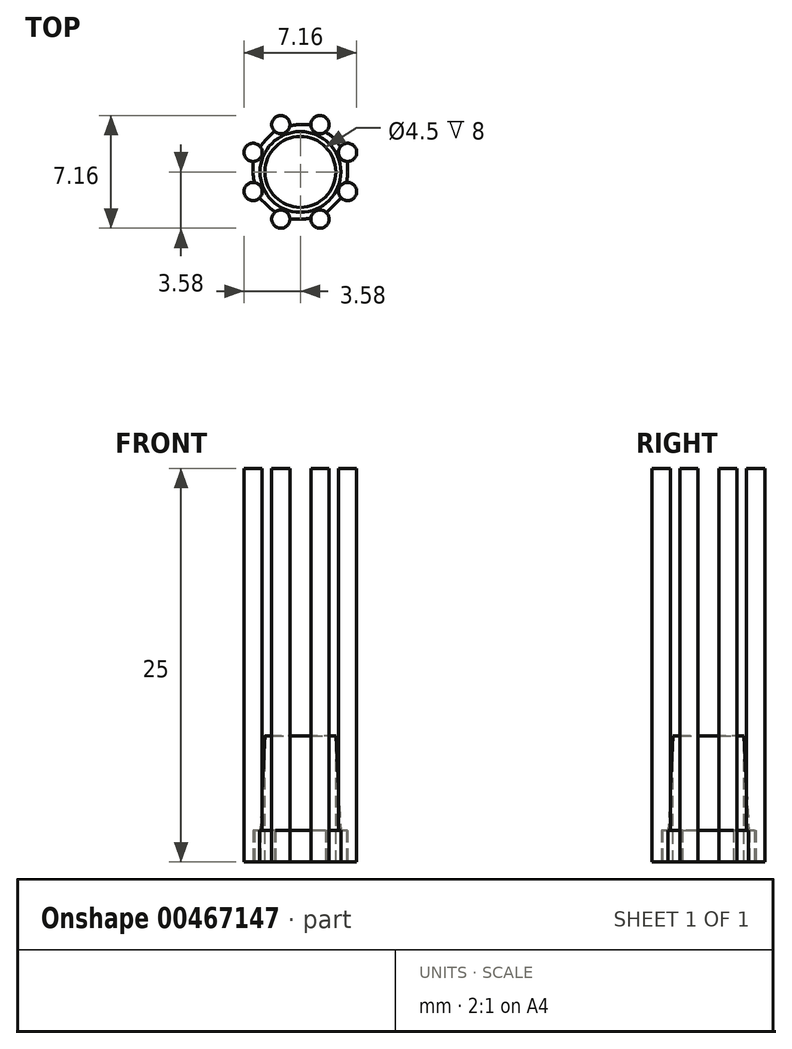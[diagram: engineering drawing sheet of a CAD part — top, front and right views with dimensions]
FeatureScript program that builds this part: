
annotation { "Feature Type Name" : "Feature", "Feature Type Description" : "" }
export const myFeature = defineFeature(function(context is Context, id is Id, definition is map)
    precondition{}
    {
        {
            var Q0;
            Q0=qCreatedBy(makeId("Top.planeOp"),FACE);
            var sketch = newSketch(context, id + "F0", { "sketchPlane" : qUnion([Q0])});
            skCircle(sketch, "E0", {"center": v(0, 0) * mm, "radius": 2.25 * mm});
            skSolve(sketch);
        }
        {
            var Q0;
            Q0=makeQuery(id+"F0.imprint","IMPRINT",FACE,{"disambiguationData":[TD([[makeQuery(id+"F0.imprint","IMPRINT",EDGE,{"derivedFrom":sQuery(id+"F0.wireOp",EDGE,"E0")}),1.0]])]});
            extrude(context, id + "F1", {"entities" : qUnion([Q0]), "oppositeDirection" : true, "depth" : 8 * mm, "offsetDistance" : 25 * mm, "hasDraft" : true, "draftAngle" : 3 * degree});
        }
        {
            var Q0;
            Q0=makeQuery(id+"F1.opExtrude","CAP_FACE",FACE,{"disambiguationData":[OSD([sQuery(id+"F0.wireOp",EDGE,"E0")])],"isStart":false});
            var sketch = newSketch(context, id + "F2", { "sketchPlane" : qUnion([Q0])});
            skCircle(sketch, "E1", {"center": v(0, 0) * mm, "radius": 3 * mm});
            skCircle(sketch, "E2.cCircle", {"center": v(0, 0) * mm, "radius": 3 * mm, "construction": true});
            skLineSegment(sketch, "E2.0", {"start": v(-1.24, -3) * mm, "end": v(-3, -1.24) * mm});
            skLineSegment(sketch, "E2.1", {"start": v(-3, -1.24) * mm, "end": v(-3, 1.24) * mm});
            skLineSegment(sketch, "E2.2", {"start": v(-3, 1.24) * mm, "end": v(-1.24, 3) * mm});
            skLineSegment(sketch, "E2.3", {"start": v(-1.24, 3) * mm, "end": v(1.24, 3) * mm});
            skLineSegment(sketch, "E2.4", {"start": v(1.24, 3) * mm, "end": v(3, 1.24) * mm});
            skLineSegment(sketch, "E2.5", {"start": v(3, 1.24) * mm, "end": v(3, -1.24) * mm});
            skLineSegment(sketch, "E2.6", {"start": v(3, -1.24) * mm, "end": v(1.24, -3) * mm});
            skLineSegment(sketch, "E2.7", {"start": v(1.24, -3) * mm, "end": v(-1.24, -3) * mm});
            skPoint(sketch, "E2.0.midPoint", {"position": v(-2.12, -2.12) * mm});
            skCircle(sketch, "E3", {"center": v(3, 1.24) * mm, "radius": 0.58 * mm});
            skCircle(sketch, "E4", {"center": v(1.24, 3) * mm, "radius": 0.58 * mm});
            skCircle(sketch, "E5", {"center": v(-1.24, 3) * mm, "radius": 0.58 * mm});
            skCircle(sketch, "E6", {"center": v(-3, 1.24) * mm, "radius": 0.58 * mm});
            skCircle(sketch, "E7", {"center": v(-3, -1.24) * mm, "radius": 0.58 * mm});
            skCircle(sketch, "E8", {"center": v(-1.24, -3) * mm, "radius": 0.58 * mm});
            skCircle(sketch, "E9", {"center": v(1.24, -3) * mm, "radius": 0.58 * mm});
            skCircle(sketch, "E10", {"center": v(3, -1.24) * mm, "radius": 0.58 * mm});
            skSolve(sketch);
        }
        {
            var Q0;
            Q0=makeQuery(id+"F2.imprint","IMPRINT",FACE,{"disambiguationData":[TD([[makeQuery(id+"F2.imprint","IMPRINT",EDGE,{"derivedFrom":sQuery(id+"F2.wireOp",EDGE,"E1")}),1.0]])]});
            var Q1;
            Q1=makeQuery(id+"F2.imprint","IMPRINT",FACE,{"disambiguationData":[TD([[makeQuery(id+"F2.imprint","IMPRINT",EDGE,{"derivedFrom":makeQuery(id+"F1.opExtrude","CAP_EDGE",EDGE,{"disambiguationData":[OSD([sQuery(id+"F0.wireOp",EDGE,"E0")])],"isStart":false})}),-1.0]])]});
            var Q2;
            {var subQ0=sQuery(id+"F2.wireOp",EDGE,"E2.4");var subQ1=sQuery(id+"F2.wireOp",EDGE,"E1");var subQ2=makeQuery(id+"F2.imprint","INTERSECT",VERTEX,{"derivedFrom":[subQ1,subQ0]});Q2=makeQuery(id+"F2.imprint","IMPRINT",FACE,{"disambiguationData":[TD([[makeQuery(id+"F2.imprint","IMPRINT",EDGE,{"disambiguationData":[TD([[subQ2,-1.0]])],"derivedFrom":subQ1}),-1.0]])]});}
            var Q3;
            {var subQ0=sQuery(id+"F2.wireOp",EDGE,"E2.3");var subQ1=sQuery(id+"F2.wireOp",EDGE,"E1");var subQ2=makeQuery(id+"F2.imprint","INTERSECT",VERTEX,{"derivedFrom":[subQ1,subQ0]});Q3=makeQuery(id+"F2.imprint","IMPRINT",FACE,{"disambiguationData":[TD([[makeQuery(id+"F2.imprint","IMPRINT",EDGE,{"disambiguationData":[TD([[subQ2,-1.0]])],"derivedFrom":subQ1}),-1.0]])]});}
            var Q4;
            {var subQ0=sQuery(id+"F2.wireOp",EDGE,"E2.2");var subQ1=sQuery(id+"F2.wireOp",EDGE,"E1");var subQ2=makeQuery(id+"F2.imprint","INTERSECT",VERTEX,{"derivedFrom":[subQ1,subQ0]});Q4=makeQuery(id+"F2.imprint","IMPRINT",FACE,{"disambiguationData":[TD([[makeQuery(id+"F2.imprint","IMPRINT",EDGE,{"disambiguationData":[TD([[subQ2,-1.0]])],"derivedFrom":subQ1}),-1.0]])]});}
            var Q5;
            {var subQ0=sQuery(id+"F2.wireOp",EDGE,"E2.1");var subQ1=sQuery(id+"F2.wireOp",EDGE,"E1");var subQ2=makeQuery(id+"F2.imprint","INTERSECT",VERTEX,{"derivedFrom":[subQ1,subQ0]});Q5=makeQuery(id+"F2.imprint","IMPRINT",FACE,{"disambiguationData":[TD([[makeQuery(id+"F2.imprint","IMPRINT",EDGE,{"disambiguationData":[TD([[subQ2,-1.0]])],"derivedFrom":subQ1}),-1.0]])]});}
            var Q6;
            {var subQ0=sQuery(id+"F2.wireOp",EDGE,"E2.0");var subQ1=sQuery(id+"F2.wireOp",EDGE,"E1");var subQ2=makeQuery(id+"F2.imprint","INTERSECT",VERTEX,{"derivedFrom":[subQ1,subQ0]});Q6=makeQuery(id+"F2.imprint","IMPRINT",FACE,{"disambiguationData":[TD([[makeQuery(id+"F2.imprint","IMPRINT",EDGE,{"disambiguationData":[TD([[subQ2,-1.0]])],"derivedFrom":subQ1}),-1.0]])]});}
            var Q7;
            {var subQ0=sQuery(id+"F2.wireOp",EDGE,"E2.7");var subQ1=sQuery(id+"F2.wireOp",EDGE,"E1");var subQ2=makeQuery(id+"F2.imprint","INTERSECT",VERTEX,{"derivedFrom":[subQ1,subQ0]});Q7=makeQuery(id+"F2.imprint","IMPRINT",FACE,{"disambiguationData":[TD([[makeQuery(id+"F2.imprint","IMPRINT",EDGE,{"disambiguationData":[TD([[subQ2,-1.0]])],"derivedFrom":subQ1}),-1.0]])]});}
            var Q8;
            {var subQ0=sQuery(id+"F2.wireOp",EDGE,"E2.5");var subQ1=sQuery(id+"F2.wireOp",EDGE,"E1");var subQ2=makeQuery(id+"F2.imprint","INTERSECT",VERTEX,{"derivedFrom":[subQ1,subQ0]});Q8=makeQuery(id+"F2.imprint","IMPRINT",FACE,{"disambiguationData":[TD([[makeQuery(id+"F2.imprint","IMPRINT",EDGE,{"disambiguationData":[TD([[subQ2,1.0]])],"derivedFrom":subQ1}),-1.0]])]});}
            var Q9;
            {var subQ0=sQuery(id+"F2.wireOp",EDGE,"E2.4");var subQ1=sQuery(id+"F2.wireOp",EDGE,"E1");var subQ2=makeQuery(id+"F2.imprint","INTERSECT",VERTEX,{"derivedFrom":[subQ1,subQ0]});Q9=makeQuery(id+"F2.imprint","IMPRINT",FACE,{"disambiguationData":[TD([[makeQuery(id+"F2.imprint","IMPRINT",EDGE,{"disambiguationData":[TD([[subQ2,1.0]])],"derivedFrom":subQ1}),-1.0]])]});}
            var Q10;
            Q10=makeQuery(id+"F1.opExtrude","CAP_FACE",FACE,{"disambiguationData":[OSD([sQuery(id+"F0.wireOp",EDGE,"E0")])],"isStart":false});
            extrude(context, id + "F3", {"entities" : qUnion([Q0, Q1, Q2, Q3, Q4, Q5, Q6, Q7, Q8, Q9]), "operationType" : NewBodyOperationType.ADD, "oppositeDirection" : true, "depth" : 2 * mm, "endBoundEntityFace" : qUnion([Q10]), "offsetDistance" : 25 * mm});
        }
        {
            var Q0;
            Q0=makeQuery(id+"F0.imprint","IMPRINT",FACE,{"disambiguationData":[TD([[makeQuery(id+"F0.imprint","IMPRINT",EDGE,{"derivedFrom":sQuery(id+"F0.wireOp",EDGE,"E0")}),1.0]])]});
            extrude(context, id + "F4", {"entities" : qUnion([Q0]), "operationType" : NewBodyOperationType.REMOVE, "endBound" : BoundingType.THROUGH_ALL, "oppositeDirection" : true, "depth" : 25 * mm, "offsetDistance" : 25 * mm});
        }
        {
            var Q0;
            {var subQ0=sQuery(id+"F2.wireOp",EDGE,"E2.4");var subQ1=sQuery(id+"F2.wireOp",EDGE,"E2.3");var subQ2=makeQuery(id+"F2.imprint","INTERSECT",VERTEX,{"derivedFrom":[subQ1,subQ0]});Q0=makeQuery(id+"F2.imprint","IMPRINT",FACE,{"disambiguationData":[TD([[makeQuery(id+"F2.imprint","IMPRINT",EDGE,{"disambiguationData":[TD([[subQ2,1.0]])],"derivedFrom":subQ1}),1.0]])]});}
            var Q1;
            {var subQ0=sQuery(id+"F2.wireOp",EDGE,"E4");var subQ3=sQuery(id+"F2.wireOp",EDGE,"E1");var subQ8=makeQuery(id+"F2.imprint","INTERSECT",VERTEX,{"disambiguationData":[OD(0.0)],"derivedFrom":[subQ3,subQ0]});Q1=makeQuery(id+"F2.imprint","IMPRINT",FACE,{"disambiguationData":[TD([[makeQuery(id+"F2.imprint","IMPRINT",EDGE,{"disambiguationData":[TD([[subQ8,-1.0]])],"derivedFrom":subQ3}),-1.0]])]});}
            var Q2;
            {var subQ0=sQuery(id+"F2.wireOp",EDGE,"E4");var subQ1=sQuery(id+"F2.wireOp",EDGE,"E1");var subQ2=makeQuery(id+"F2.imprint","INTERSECT",VERTEX,{"disambiguationData":[OD(0.0)],"derivedFrom":[subQ1,subQ0]});Q2=makeQuery(id+"F2.imprint","IMPRINT",FACE,{"disambiguationData":[TD([[makeQuery(id+"F2.imprint","IMPRINT",EDGE,{"disambiguationData":[TD([[subQ2,-1.0]])],"derivedFrom":subQ1}),1.0]])]});}
            var Q3;
            {var subQ0=sQuery(id+"F2.wireOp",EDGE,"E2.5");var subQ1=sQuery(id+"F2.wireOp",EDGE,"E2.4");var subQ2=makeQuery(id+"F2.imprint","INTERSECT",VERTEX,{"derivedFrom":[subQ1,subQ0]});Q3=makeQuery(id+"F2.imprint","IMPRINT",FACE,{"disambiguationData":[TD([[makeQuery(id+"F2.imprint","IMPRINT",EDGE,{"disambiguationData":[TD([[subQ2,1.0]])],"derivedFrom":subQ1}),1.0]])]});}
            var Q4;
            {var subQ3=sQuery(id+"F2.wireOp",EDGE,"E3");var subQ6=sQuery(id+"F2.wireOp",EDGE,"E1");var subQ8=makeQuery(id+"F2.imprint","INTERSECT",VERTEX,{"disambiguationData":[OD(0.0)],"derivedFrom":[subQ6,subQ3]});Q4=makeQuery(id+"F2.imprint","IMPRINT",FACE,{"disambiguationData":[TD([[makeQuery(id+"F2.imprint","IMPRINT",EDGE,{"disambiguationData":[TD([[subQ8,-1.0]])],"derivedFrom":subQ6}),-1.0]])]});}
            var Q5;
            {var subQ0=sQuery(id+"F2.wireOp",EDGE,"E3");var subQ1=sQuery(id+"F2.wireOp",EDGE,"E1");var subQ2=makeQuery(id+"F2.imprint","INTERSECT",VERTEX,{"disambiguationData":[OD(0.0)],"derivedFrom":[subQ1,subQ0]});Q5=makeQuery(id+"F2.imprint","IMPRINT",FACE,{"disambiguationData":[TD([[makeQuery(id+"F2.imprint","IMPRINT",EDGE,{"disambiguationData":[TD([[subQ2,-1.0]])],"derivedFrom":subQ1}),1.0]])]});}
            var Q6;
            {var subQ0=sQuery(id+"F2.wireOp",EDGE,"E2.3");var subQ1=sQuery(id+"F2.wireOp",EDGE,"E2.2");var subQ2=makeQuery(id+"F2.imprint","INTERSECT",VERTEX,{"derivedFrom":[subQ1,subQ0]});Q6=makeQuery(id+"F2.imprint","IMPRINT",FACE,{"disambiguationData":[TD([[makeQuery(id+"F2.imprint","IMPRINT",EDGE,{"disambiguationData":[TD([[subQ2,1.0]])],"derivedFrom":subQ1}),1.0]])]});}
            var Q7;
            {var subQ3=sQuery(id+"F2.wireOp",EDGE,"E5");var subQ6=sQuery(id+"F2.wireOp",EDGE,"E1");var subQ8=makeQuery(id+"F2.imprint","INTERSECT",VERTEX,{"disambiguationData":[OD(0.0)],"derivedFrom":[subQ6,subQ3]});Q7=makeQuery(id+"F2.imprint","IMPRINT",FACE,{"disambiguationData":[TD([[makeQuery(id+"F2.imprint","IMPRINT",EDGE,{"disambiguationData":[TD([[subQ8,-1.0]])],"derivedFrom":subQ6}),-1.0]])]});}
            var Q8;
            {var subQ0=sQuery(id+"F2.wireOp",EDGE,"E5");var subQ1=sQuery(id+"F2.wireOp",EDGE,"E1");var subQ2=makeQuery(id+"F2.imprint","INTERSECT",VERTEX,{"disambiguationData":[OD(0.0)],"derivedFrom":[subQ1,subQ0]});Q8=makeQuery(id+"F2.imprint","IMPRINT",FACE,{"disambiguationData":[TD([[makeQuery(id+"F2.imprint","IMPRINT",EDGE,{"disambiguationData":[TD([[subQ2,-1.0]])],"derivedFrom":subQ1}),1.0]])]});}
            var Q9;
            {var subQ0=sQuery(id+"F2.wireOp",EDGE,"E2.2");var subQ1=sQuery(id+"F2.wireOp",EDGE,"E2.1");var subQ2=makeQuery(id+"F2.imprint","INTERSECT",VERTEX,{"derivedFrom":[subQ1,subQ0]});Q9=makeQuery(id+"F2.imprint","IMPRINT",FACE,{"disambiguationData":[TD([[makeQuery(id+"F2.imprint","IMPRINT",EDGE,{"disambiguationData":[TD([[subQ2,1.0]])],"derivedFrom":subQ1}),1.0]])]});}
            var Q10;
            {var subQ3=sQuery(id+"F2.wireOp",EDGE,"E6");var subQ5=sQuery(id+"F2.wireOp",EDGE,"E1");var subQ6=makeQuery(id+"F2.imprint","INTERSECT",VERTEX,{"disambiguationData":[OD(0.0)],"derivedFrom":[subQ5,subQ3]});Q10=makeQuery(id+"F2.imprint","IMPRINT",FACE,{"disambiguationData":[TD([[makeQuery(id+"F2.imprint","IMPRINT",EDGE,{"disambiguationData":[TD([[subQ6,-1.0]])],"derivedFrom":subQ5}),-1.0]])]});}
            var Q11;
            {var subQ0=sQuery(id+"F2.wireOp",EDGE,"E6");var subQ1=sQuery(id+"F2.wireOp",EDGE,"E1");var subQ2=makeQuery(id+"F2.imprint","INTERSECT",VERTEX,{"disambiguationData":[OD(0.0)],"derivedFrom":[subQ1,subQ0]});Q11=makeQuery(id+"F2.imprint","IMPRINT",FACE,{"disambiguationData":[TD([[makeQuery(id+"F2.imprint","IMPRINT",EDGE,{"disambiguationData":[TD([[subQ2,-1.0]])],"derivedFrom":subQ1}),1.0]])]});}
            var Q12;
            {var subQ0=sQuery(id+"F2.wireOp",EDGE,"E2.1");var subQ1=sQuery(id+"F2.wireOp",EDGE,"E2.0");var subQ2=makeQuery(id+"F2.imprint","INTERSECT",VERTEX,{"derivedFrom":[subQ1,subQ0]});Q12=makeQuery(id+"F2.imprint","IMPRINT",FACE,{"disambiguationData":[TD([[makeQuery(id+"F2.imprint","IMPRINT",EDGE,{"disambiguationData":[TD([[subQ2,1.0]])],"derivedFrom":subQ1}),1.0]])]});}
            var Q13;
            {var subQ0=sQuery(id+"F2.wireOp",EDGE,"E7");var subQ3=sQuery(id+"F2.wireOp",EDGE,"E1");var subQ4=makeQuery(id+"F2.imprint","INTERSECT",VERTEX,{"disambiguationData":[OD(0.0)],"derivedFrom":[subQ3,subQ0]});Q13=makeQuery(id+"F2.imprint","IMPRINT",FACE,{"disambiguationData":[TD([[makeQuery(id+"F2.imprint","IMPRINT",EDGE,{"disambiguationData":[TD([[subQ4,-1.0]])],"derivedFrom":subQ3}),-1.0]])]});}
            var Q14;
            {var subQ0=sQuery(id+"F2.wireOp",EDGE,"E7");var subQ1=sQuery(id+"F2.wireOp",EDGE,"E1");var subQ2=makeQuery(id+"F2.imprint","INTERSECT",VERTEX,{"disambiguationData":[OD(0.0)],"derivedFrom":[subQ1,subQ0]});Q14=makeQuery(id+"F2.imprint","IMPRINT",FACE,{"disambiguationData":[TD([[makeQuery(id+"F2.imprint","IMPRINT",EDGE,{"disambiguationData":[TD([[subQ2,-1.0]])],"derivedFrom":subQ1}),1.0]])]});}
            var Q15;
            {var subQ0=sQuery(id+"F2.wireOp",EDGE,"E2.7");var subQ1=sQuery(id+"F2.wireOp",EDGE,"E2.0");var subQ2=makeQuery(id+"F2.imprint","INTERSECT",VERTEX,{"derivedFrom":[subQ1,subQ0]});Q15=makeQuery(id+"F2.imprint","IMPRINT",FACE,{"disambiguationData":[TD([[makeQuery(id+"F2.imprint","IMPRINT",EDGE,{"disambiguationData":[TD([[subQ2,-1.0]])],"derivedFrom":subQ1}),1.0]])]});}
            var Q16;
            {var subQ3=sQuery(id+"F2.wireOp",EDGE,"E8");var subQ6=sQuery(id+"F2.wireOp",EDGE,"E1");var subQ8=makeQuery(id+"F2.imprint","INTERSECT",VERTEX,{"disambiguationData":[OD(0.0)],"derivedFrom":[subQ6,subQ3]});Q16=makeQuery(id+"F2.imprint","IMPRINT",FACE,{"disambiguationData":[TD([[makeQuery(id+"F2.imprint","IMPRINT",EDGE,{"disambiguationData":[TD([[subQ8,-1.0]])],"derivedFrom":subQ6}),-1.0]])]});}
            var Q17;
            {var subQ0=sQuery(id+"F2.wireOp",EDGE,"E8");var subQ1=sQuery(id+"F2.wireOp",EDGE,"E1");var subQ2=makeQuery(id+"F2.imprint","INTERSECT",VERTEX,{"disambiguationData":[OD(0.0)],"derivedFrom":[subQ1,subQ0]});Q17=makeQuery(id+"F2.imprint","IMPRINT",FACE,{"disambiguationData":[TD([[makeQuery(id+"F2.imprint","IMPRINT",EDGE,{"disambiguationData":[TD([[subQ2,-1.0]])],"derivedFrom":subQ1}),1.0]])]});}
            var Q18;
            {var subQ0=sQuery(id+"F2.wireOp",EDGE,"E2.7");var subQ1=sQuery(id+"F2.wireOp",EDGE,"E2.6");var subQ2=makeQuery(id+"F2.imprint","INTERSECT",VERTEX,{"derivedFrom":[subQ1,subQ0]});Q18=makeQuery(id+"F2.imprint","IMPRINT",FACE,{"disambiguationData":[TD([[makeQuery(id+"F2.imprint","IMPRINT",EDGE,{"disambiguationData":[TD([[subQ2,1.0]])],"derivedFrom":subQ1}),1.0]])]});}
            var Q19;
            {var subQ3=sQuery(id+"F2.wireOp",EDGE,"E9");var subQ5=sQuery(id+"F2.wireOp",EDGE,"E1");var subQ6=makeQuery(id+"F2.imprint","INTERSECT",VERTEX,{"disambiguationData":[OD(0.0)],"derivedFrom":[subQ5,subQ3]});Q19=makeQuery(id+"F2.imprint","IMPRINT",FACE,{"disambiguationData":[TD([[makeQuery(id+"F2.imprint","IMPRINT",EDGE,{"disambiguationData":[TD([[subQ6,-1.0]])],"derivedFrom":subQ5}),-1.0]])]});}
            var Q20;
            {var subQ0=sQuery(id+"F2.wireOp",EDGE,"E9");var subQ1=sQuery(id+"F2.wireOp",EDGE,"E1");var subQ2=makeQuery(id+"F2.imprint","INTERSECT",VERTEX,{"disambiguationData":[OD(0.0)],"derivedFrom":[subQ1,subQ0]});Q20=makeQuery(id+"F2.imprint","IMPRINT",FACE,{"disambiguationData":[TD([[makeQuery(id+"F2.imprint","IMPRINT",EDGE,{"disambiguationData":[TD([[subQ2,-1.0]])],"derivedFrom":subQ1}),1.0]])]});}
            var Q21;
            {var subQ0=sQuery(id+"F2.wireOp",EDGE,"E10");var subQ1=sQuery(id+"F2.wireOp",EDGE,"E1");var subQ2=makeQuery(id+"F2.imprint","INTERSECT",VERTEX,{"disambiguationData":[OD(0.0)],"derivedFrom":[subQ1,subQ0]});Q21=makeQuery(id+"F2.imprint","IMPRINT",FACE,{"disambiguationData":[TD([[makeQuery(id+"F2.imprint","IMPRINT",EDGE,{"disambiguationData":[TD([[subQ2,-1.0]])],"derivedFrom":subQ1}),1.0]])]});}
            var Q22;
            {var subQ0=sQuery(id+"F2.wireOp",EDGE,"E10");var subQ3=sQuery(id+"F2.wireOp",EDGE,"E1");var subQ8=makeQuery(id+"F2.imprint","INTERSECT",VERTEX,{"disambiguationData":[OD(0.0)],"derivedFrom":[subQ3,subQ0]});Q22=makeQuery(id+"F2.imprint","IMPRINT",FACE,{"disambiguationData":[TD([[makeQuery(id+"F2.imprint","IMPRINT",EDGE,{"disambiguationData":[TD([[subQ8,-1.0]])],"derivedFrom":subQ3}),-1.0]])]});}
            var Q23;
            {var subQ0=sQuery(id+"F2.wireOp",EDGE,"E2.6");var subQ1=sQuery(id+"F2.wireOp",EDGE,"E2.5");var subQ2=makeQuery(id+"F2.imprint","INTERSECT",VERTEX,{"derivedFrom":[subQ1,subQ0]});Q23=makeQuery(id+"F2.imprint","IMPRINT",FACE,{"disambiguationData":[TD([[makeQuery(id+"F2.imprint","IMPRINT",EDGE,{"disambiguationData":[TD([[subQ2,1.0]])],"derivedFrom":subQ1}),1.0]])]});}
            extrude(context, id + "F5", {"entities" : qUnion([Q0, Q1, Q2, Q3, Q4, Q5, Q6, Q7, Q8, Q9, Q10, Q11, Q12, Q13, Q14, Q15, Q16, Q17, Q18, Q19, Q20, Q21, Q22, Q23]), "operationType" : NewBodyOperationType.ADD, "oppositeDirection" : true, "depth" : 25 * mm, "offsetDistance" : 25 * mm});
        }
    });
